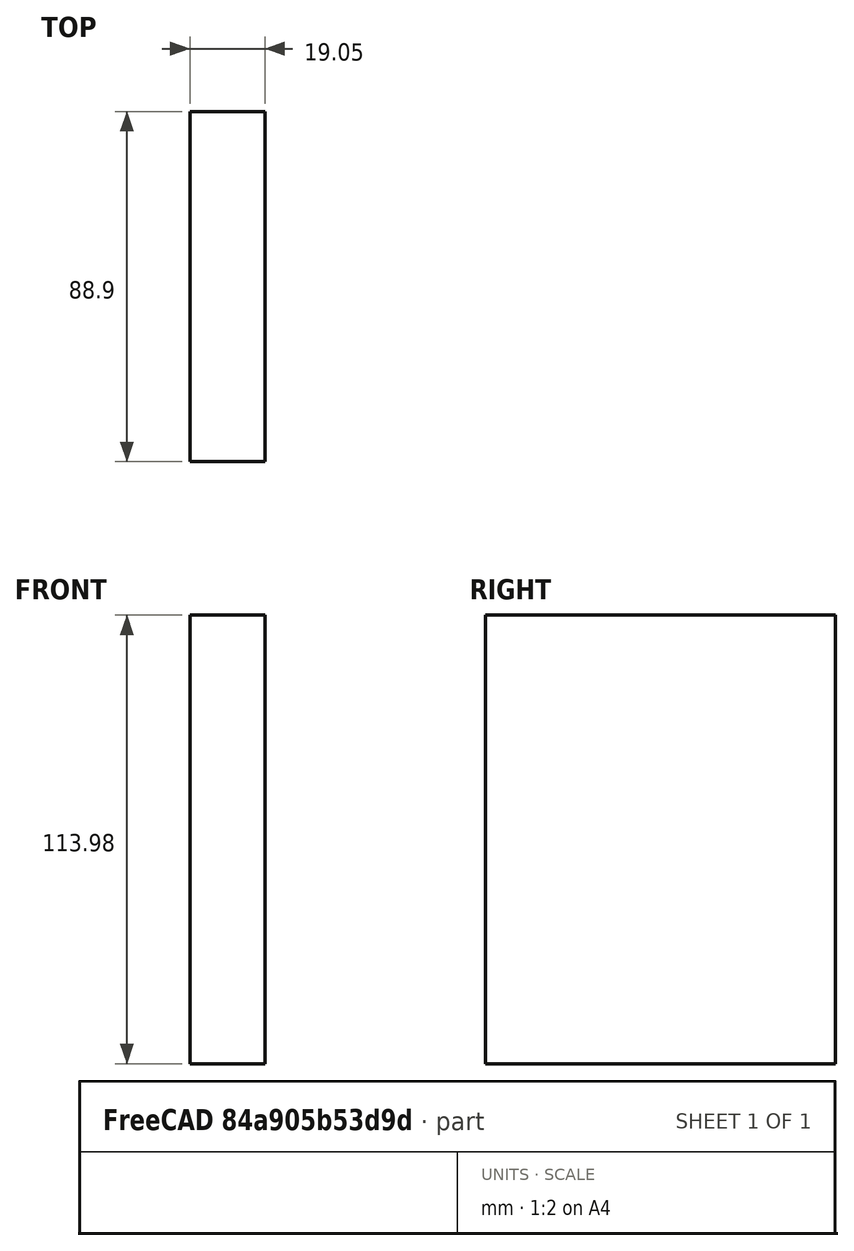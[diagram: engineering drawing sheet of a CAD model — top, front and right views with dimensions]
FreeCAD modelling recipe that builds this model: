
FCSTD DOCUMENT  (FreeCAD 0.19R24291 (Git))
Label: leg
License: All rights reserved
LicenseURL: http://en.wikipedia.org/wiki/All_rights_reserved
objects: Sketcher::SketchObject×1, PartDesign::Pad×1, PartDesign::Body×1
note: 4 computed .brp shape members not serialized (recipe doc carries the construction recipe); baked Part::Feature solids carry a one-line shape summary decoded from their .brp

FEATURE [Sketcher::SketchObject] Sketch
  FullyConstrained = true
  MapMode = 5
  Support = -> [XY_Plane]
  expr: Constraints[10] = 3.5 * 25.4
  expr: Constraints[9] = 3 / 4 * 25.4
  sketch-geometry (4):
    g0: LineSegment StartX=0 StartY=0 StartZ=0 EndX=19.05 EndY=0 EndZ=0
    g1: LineSegment StartX=19.05 StartY=0 StartZ=0 EndX=19.05 EndY=88.9 EndZ=0
    g2: LineSegment StartX=19.05 StartY=88.9 StartZ=0 EndX=0 EndY=88.9 EndZ=0
    g3: LineSegment StartX=0 StartY=88.9 StartZ=0 EndX=0 EndY=0 EndZ=0
  constraints (11):
    c: Coincident(g0,g1)
    c: Coincident(g1,g2)
    c: Coincident(g2,g3)
    c: Coincident(g3,g0)
    c: Horizontal(g0)
    c: Horizontal(g2)
    c: Vertical(g1)
    c: Vertical(g3)
    c: Coincident(g0,g-1)
    c: DistanceX(g0,g0) = 19.05
    c: DistanceY(g3,g3) = 88.9
FEATURE [PartDesign::Pad] Pad
  Direction = (1,1,1)
  Length = 113.98
  Length2 = 100
  Profile = -> Sketch
  Type = 0
  expr: Length = 19.08 + 6 + 88.90000000000001
FEATURE [PartDesign::Body] Body
  Group = -> [Sketch,Pad]
  Origin = -> Origin
  Tip = -> Pad
